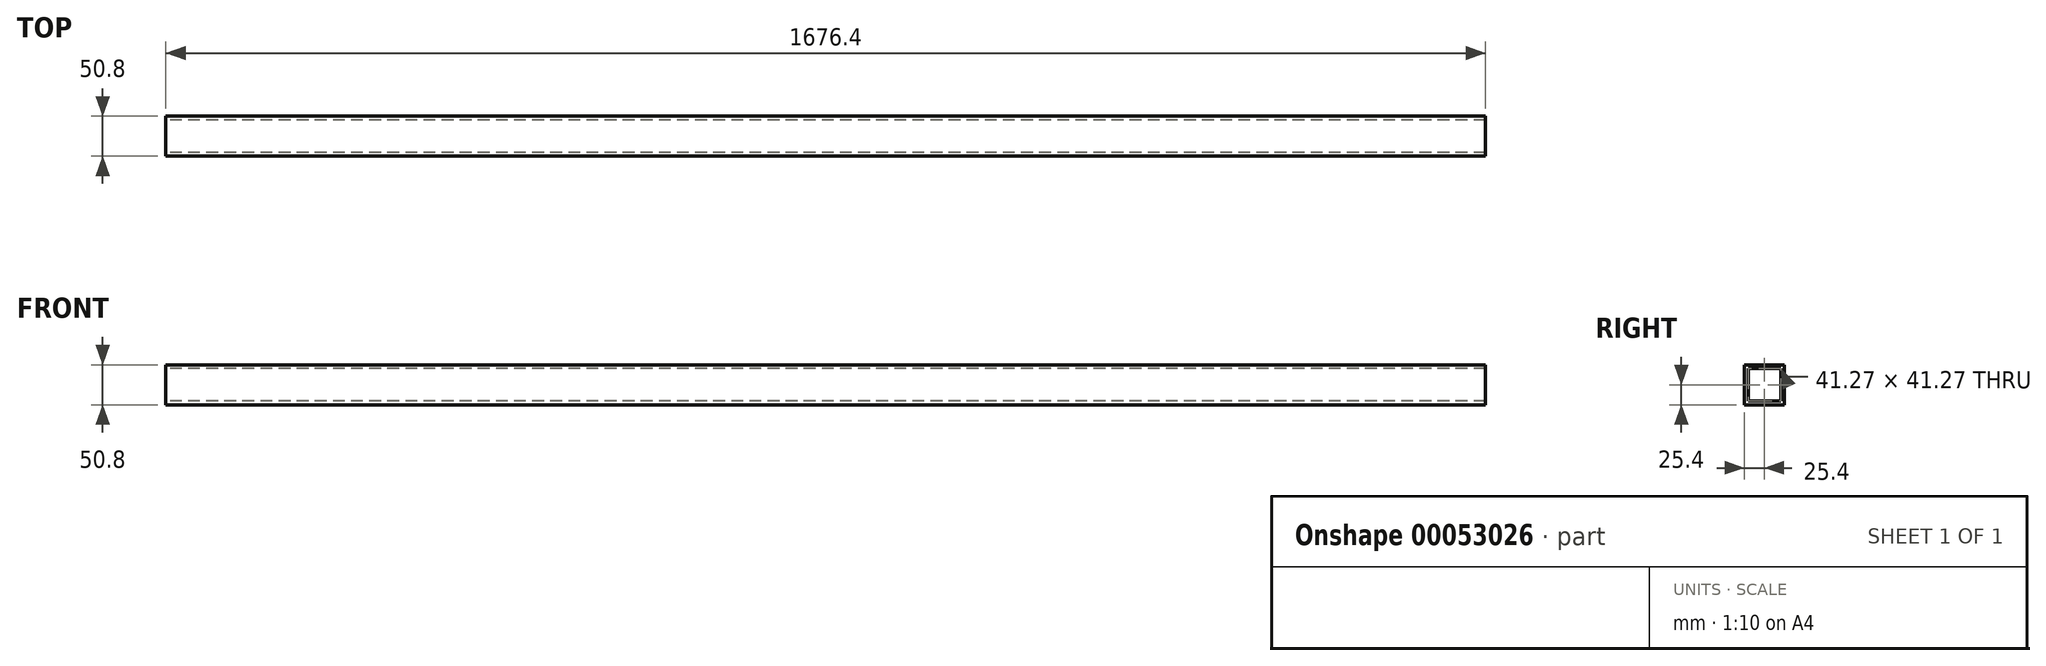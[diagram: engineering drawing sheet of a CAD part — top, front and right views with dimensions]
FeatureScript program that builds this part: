
annotation { "Feature Type Name" : "Feature", "Feature Type Description" : "" }
export const myFeature = defineFeature(function(context is Context, id is Id, definition is map)
    precondition{}
    {
        {
            var Q0;
            Q0=qCreatedBy(makeId("Right.planeOp"),FACE);
            var sketch = newSketch(context, id + "F0", { "sketchPlane" : qUnion([Q0])});
            skLineSegment(sketch, "E0.bottom", {"start": v(0, 0) * mm, "end": v(-50.8, 0) * mm});
            skLineSegment(sketch, "E0.top", {"start": v(0, 50.8) * mm, "end": v(-50.8, 50.8) * mm});
            skLineSegment(sketch, "E0.left", {"start": v(0, 0) * mm, "end": v(0, 50.8) * mm});
            skLineSegment(sketch, "E0.right", {"start": v(-50.8, 0) * mm, "end": v(-50.8, 50.8) * mm});
            skLineSegment(sketch, "E1.bottom", {"start": v(-4.76, 4.76) * mm, "end": v(-46.04, 4.76) * mm});
            skLineSegment(sketch, "E1.top", {"start": v(-4.76, 46.04) * mm, "end": v(-46.04, 46.04) * mm});
            skLineSegment(sketch, "E1.left", {"start": v(-4.76, 4.76) * mm, "end": v(-4.76, 46.04) * mm});
            skLineSegment(sketch, "E1.right", {"start": v(-46.04, 4.76) * mm, "end": v(-46.04, 46.04) * mm});
            skSolve(sketch);
        }
        {
            var Q0;
            Q0=makeQuery(id+"F0.imprint","IMPRINT",FACE,{"disambiguationData":[TD([[makeQuery(id+"F0.imprint","IMPRINT",EDGE,{"derivedFrom":sQuery(id+"F0.wireOp",EDGE,"E0.bottom")}),-1.0]])]});
            extrude(context, id + "F1", {"entities" : qUnion([Q0]), "depth" : 1676.4 * mm});
        }
    });
